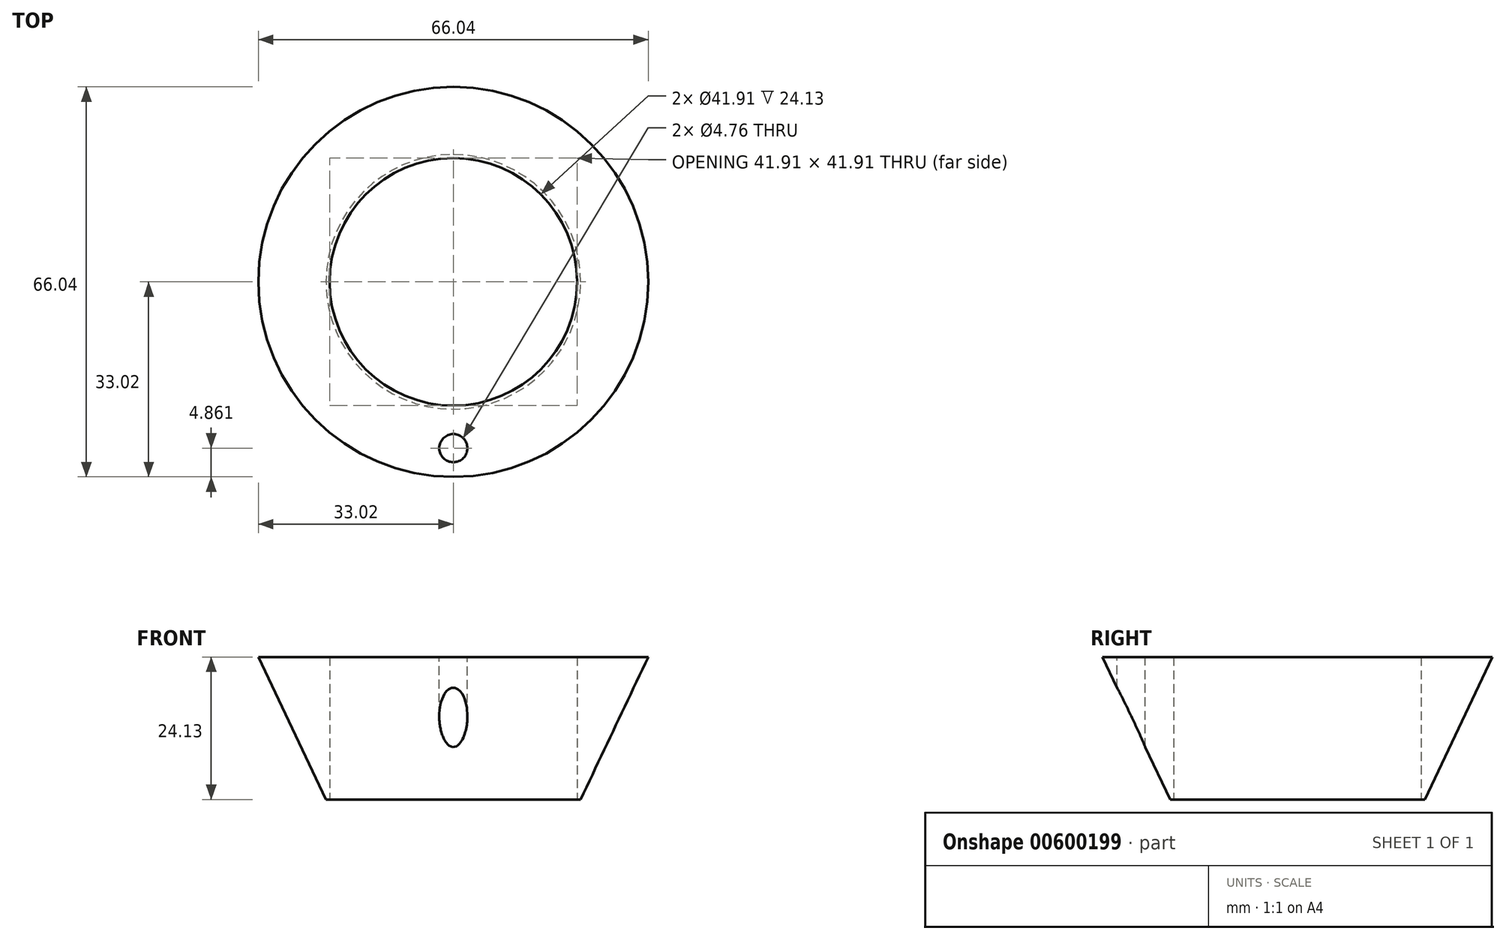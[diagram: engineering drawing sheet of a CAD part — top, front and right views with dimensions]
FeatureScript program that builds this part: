
annotation { "Feature Type Name" : "Feature", "Feature Type Description" : "" }
export const myFeature = defineFeature(function(context is Context, id is Id, definition is map)
    precondition{}
    {
        {
            var Q0;
            Q0=qCreatedBy(makeId("Front.planeOp"),FACE);
            var sketch = newSketch(context, id + "F0", { "sketchPlane" : qUnion([Q0])});
            skLineSegment(sketch, "E0", {"start": v(0, 0) * mm, "end": v(0, 48.4) * mm});
            skLineSegment(sketch, "E1", {"start": v(20.96, 25.4) * mm, "end": v(20.96, 0) * mm});
            skLineSegment(sketch, "E2", {"start": v(20.95, 0) * mm, "end": v(33.02, 25.4) * mm});
            skLineSegment(sketch, "E3", {"start": v(33.02, 25.4) * mm, "end": v(20.96, 25.4) * mm});
            skLineSegment(sketch, "E4.bottom", {"start": v(32.26, 25.4) * mm, "end": v(30.67, 25.4) * mm});
            skLineSegment(sketch, "E4.top", {"start": v(32.26, 38.1) * mm, "end": v(30.67, 38.1) * mm});
            skLineSegment(sketch, "E4.left", {"start": v(30.67, 25.4) * mm, "end": v(30.67, 38.1) * mm});
            skLineSegment(sketch, "E4.right", {"start": v(32.26, 25.4) * mm, "end": v(32.26, 38.1) * mm});
            skSolve(sketch);
        }
        {
            var Q0;
            {var subQ1=sQuery(id+"F0.wireOp",EDGE,"E1");Q0=makeQuery(id+"F0.imprint","IMPRINT",FACE,{"disambiguationData":[TD([[makeQuery(id+"F0.imprint","IMPRINT",EDGE,{"derivedFrom":subQ1}),1.0]])]});}
            var Q1;
            Q1=makeQuery(id+"F0.imprint","IMPRINT",FACE,{"disambiguationData":[TD([[makeQuery(id+"F0.imprint","IMPRINT",EDGE,{"derivedFrom":sQuery(id+"F0.wireOp",EDGE,"E4.bottom")}),-1.0]])]});
            var Q2;
            Q2=sQuery(id+"F0.wireOp",EDGE,"E0");
            revolve(context, id + "F1", {"entities" : qUnion([Q0, Q1]), "axis" : qUnion([Q2]), "revolveType" : RevolveType.FULL});
        }
        {
            var Q0;
            {var subQ0=sQuery(id+"F0.wireOp",EDGE,"E3");Q0=makeQuery(id+"F1.opRevolve","SWEPT_FACE",FACE,{"disambiguationData":[OSD([subQ0]),TDD([makeQuery(id+"F0.imprint","IMPRINT",EDGE,{"disambiguationData":[TD([[makeQuery(id+"F0.imprint","INTERSECT",VERTEX,{"derivedFrom":[sQuery(id+"F0.wireOp",EDGE,"E1"),subQ0]}),1.0]])],"derivedFrom":subQ0})])]});}
            var sketch = newSketch(context, id + "F2", { "sketchPlane" : qUnion([Q0])});
            skCircle(sketch, "E5", {"center": v(0, -28.16) * mm, "radius": 2.38 * mm});
            skSolve(sketch);
        }
        {
            var Q0;
            Q0=makeQuery(id+"F2.imprint","IMPRINT",FACE,{"disambiguationData":[TD([[makeQuery(id+"F2.imprint","IMPRINT",EDGE,{"derivedFrom":sQuery(id+"F2.wireOp",EDGE,"E5")}),1.0]])]});
            extrude(context, id + "F3", {"entities" : qUnion([Q0]), "operationType" : NewBodyOperationType.REMOVE, "oppositeDirection" : true, "depth" : 32.97 * mm, "offsetDistance" : 25.4 * mm});
        }
        {
            var Q0;
            Q0=qCreatedBy(makeId("Top.planeOp"),FACE);
            var sketch = newSketch(context, id + "F4", { "sketchPlane" : qUnion([Q0])});
            skCircle(sketch, "E6", {"center": v(0, 0) * mm, "radius": 43.34 * mm});
            skSolve(sketch);
        }
        {
            var Q0;
            Q0=makeQuery(id+"F4.imprint","IMPRINT",FACE,{"disambiguationData":[TD([[makeQuery(id+"F4.imprint","IMPRINT",EDGE,{"derivedFrom":sQuery(id+"F4.wireOp",EDGE,"E6")}),1.0]])]});
            extrude(context, id + "F5", {"entities" : qUnion([Q0]), "operationType" : NewBodyOperationType.REMOVE, "depth" : 1.27 * mm, "offsetDistance" : 25.4 * mm});
        }
    });
